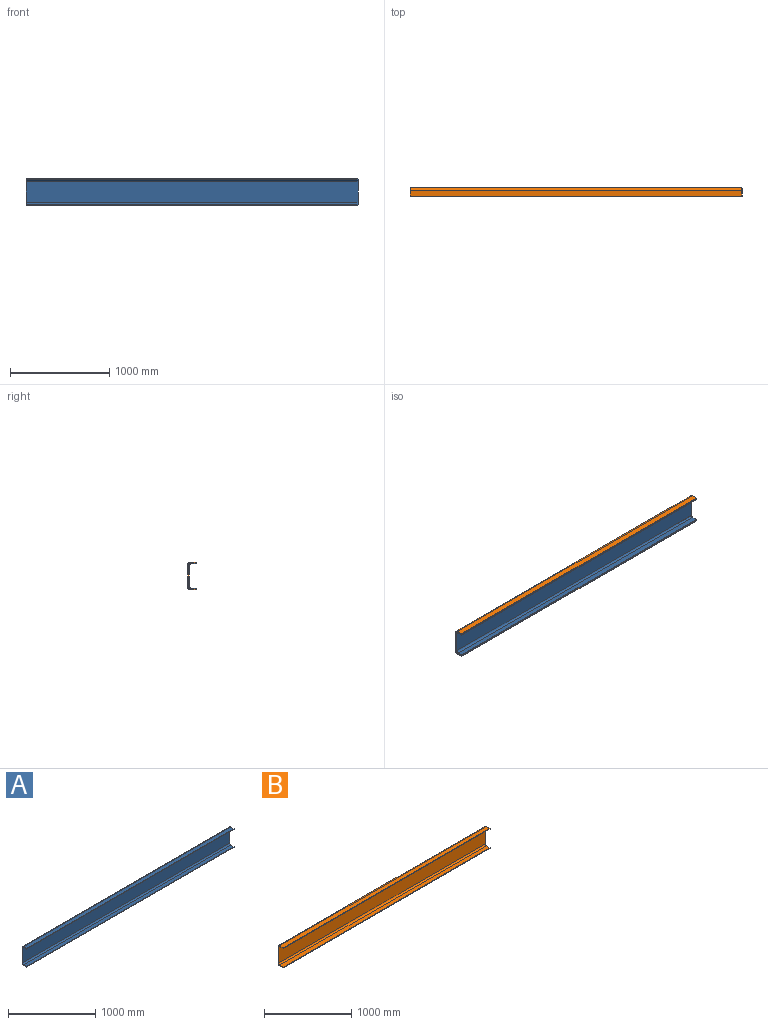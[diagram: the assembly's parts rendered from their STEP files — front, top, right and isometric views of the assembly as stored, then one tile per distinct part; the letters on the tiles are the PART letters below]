
ASSEMBLY  parts=2 mates=1
PART A: 22 faces, bbox 3352.8x76.2x260.4 mm
  f0: plane 206.38x7.94mm, normal (-1,0,0), area 1638.1mm2, adj f2,f3,f9,f19
  f1: plane 206.38x7.94mm, normal (1,0,0), area 1638.1mm2, adj f2,f3,f10,f18
  f2: plane 3352.8x206.38mm, normal (0,1,0), area 691934.1mm2, adj f0,f1,f11,f20
  f3: plane 3352.8x206.38mm, normal (0,-1,0), area 691934.1mm2, adj f0,f1,f12,f21
  f4: plane 3352.8x7.94mm, normal (0,-1,0), area 26612.9mm2, adj f5,f6,f7,f8
  f5: plane 49.21x7.94mm, normal (1,0,0), area 390.6mm2, adj f4,f7,f8,f10
  f6: plane 49.21x7.94mm, normal (-1,0,0), area 390.6mm2, adj f4,f7,f8,f9
  f7: plane 3352.8x49.21mm, normal (0,0,1), area 164999.7mm2, adj f4,f5,f6,f11
  f8: plane 3352.8x49.21mm, normal (0,0,-1), area 164999.7mm2, adj f4,f5,f6,f12
  f9: plane 26.99x26.99mm, normal (-1,0,0), area 287mm2, adj f0,f6,f11,f12
  f10: plane 26.99x26.99mm, normal (1,0,0), area 287mm2, adj f1,f5,f11,f12
  f11: cylinder r=26.99mm len=3352.8mm, axis (-1,0,0), area 142131.4mm2, adj f2,f7,f9,f10
  f12: cylinder r=19.05mm len=3352.8mm, axis (-1,0,0), area 100328.1mm2, adj f3,f8,f9,f10
  f13: plane 3352.8x7.94mm, normal (0,-1,0), area 26612.8mm2, adj f14,f15,f16,f17
  f14: plane 49.21x7.94mm, normal (-1,0,0), area 390.6mm2, adj f13,f16,f17,f19
  f15: plane 49.21x7.94mm, normal (1,0,0), area 390.6mm2, adj f13,f16,f17,f18
  f16: plane 3352.8x49.21mm, normal (0,0,-1), area 164999.7mm2, adj f13,f14,f15,f20
  f17: plane 3352.8x49.21mm, normal (0,0,1), area 164999.7mm2, adj f13,f14,f15,f21
  f18: plane 26.99x26.99mm, normal (1,0,0), area 287mm2, adj f1,f15,f20,f21
  f19: plane 26.99x26.99mm, normal (-1,0,0), area 287mm2, adj f0,f14,f20,f21
  f20: cylinder r=26.99mm len=3352.8mm, axis (1,0,0), area 142131.4mm2, adj f2,f16,f18,f19
  f21: cylinder r=19.05mm len=3352.8mm, axis (1,0,0), area 100328.1mm2, adj f3,f17,f18,f19
PART B: 22 faces, bbox 3352.8x85.7x282.6 mm
  f0: plane 225.43x9.53mm, normal (-1,0,0), area 2147.2mm2, adj f2,f3,f9,f19
  f1: plane 225.43x9.53mm, normal (1,0,0), area 2147.2mm2, adj f2,f3,f10,f18
  f2: plane 3352.8x225.43mm, normal (0,1,0), area 755804.9mm2, adj f0,f1,f11,f20
  f3: plane 3352.8x225.43mm, normal (0,-1,0), area 755804.9mm2, adj f0,f1,f12,f21
  f4: plane 3352.8x9.53mm, normal (0,-1,0), area 31935.4mm2, adj f5,f6,f7,f8
  f5: plane 57.15x9.53mm, normal (1,0,0), area 544.4mm2, adj f4,f7,f8,f10
  f6: plane 57.15x9.53mm, normal (-1,0,0), area 544.4mm2, adj f4,f7,f8,f9
  f7: plane 3352.8x57.15mm, normal (0,0,1), area 191612.5mm2, adj f4,f5,f6,f11
  f8: plane 3352.8x57.15mm, normal (0,0,-1), area 191612.5mm2, adj f4,f5,f6,f12
  f9: plane 28.58x28.58mm, normal (-1,0,0), area 356.3mm2, adj f0,f6,f11,f12
  f10: plane 28.58x28.58mm, normal (1,0,0), area 356.3mm2, adj f1,f5,f11,f12
  f11: cylinder r=28.57mm len=3352.8mm, axis (-1,0,0), area 150492.1mm2, adj f2,f7,f9,f10
  f12: cylinder r=19.05mm len=3352.8mm, axis (-1,0,0), area 100328.1mm2, adj f3,f8,f9,f10
  f13: plane 3352.8x9.53mm, normal (0,-1,0), area 31935.4mm2, adj f14,f15,f16,f17
  f14: plane 57.15x9.53mm, normal (-1,0,0), area 544.4mm2, adj f13,f16,f17,f19
  f15: plane 57.15x9.53mm, normal (1,0,0), area 544.4mm2, adj f13,f16,f17,f18
  f16: plane 3352.8x57.15mm, normal (0,0,-1), area 191612.5mm2, adj f13,f14,f15,f20
  f17: plane 3352.8x57.15mm, normal (0,0,1), area 191612.5mm2, adj f13,f14,f15,f21
  f18: plane 28.58x28.58mm, normal (1,0,0), area 356.3mm2, adj f1,f15,f20,f21
  f19: plane 28.58x28.58mm, normal (-1,0,0), area 356.3mm2, adj f0,f14,f20,f21
  f20: cylinder r=28.57mm len=3352.8mm, axis (1,0,0), area 150492.1mm2, adj f2,f16,f18,f19
  f21: cylinder r=19.05mm len=3352.8mm, axis (1,0,0), area 100328.1mm2, adj f3,f17,f18,f19
PLACE A t=(-753.79,-205.81,557.96)mm
PLACE B t=(-509.23,-196.28,-6.76)mm
MATE fastened B.f3 <-> A.f2  axis (0,-1,0) through (-804.43,-205.81,330.79)mm
